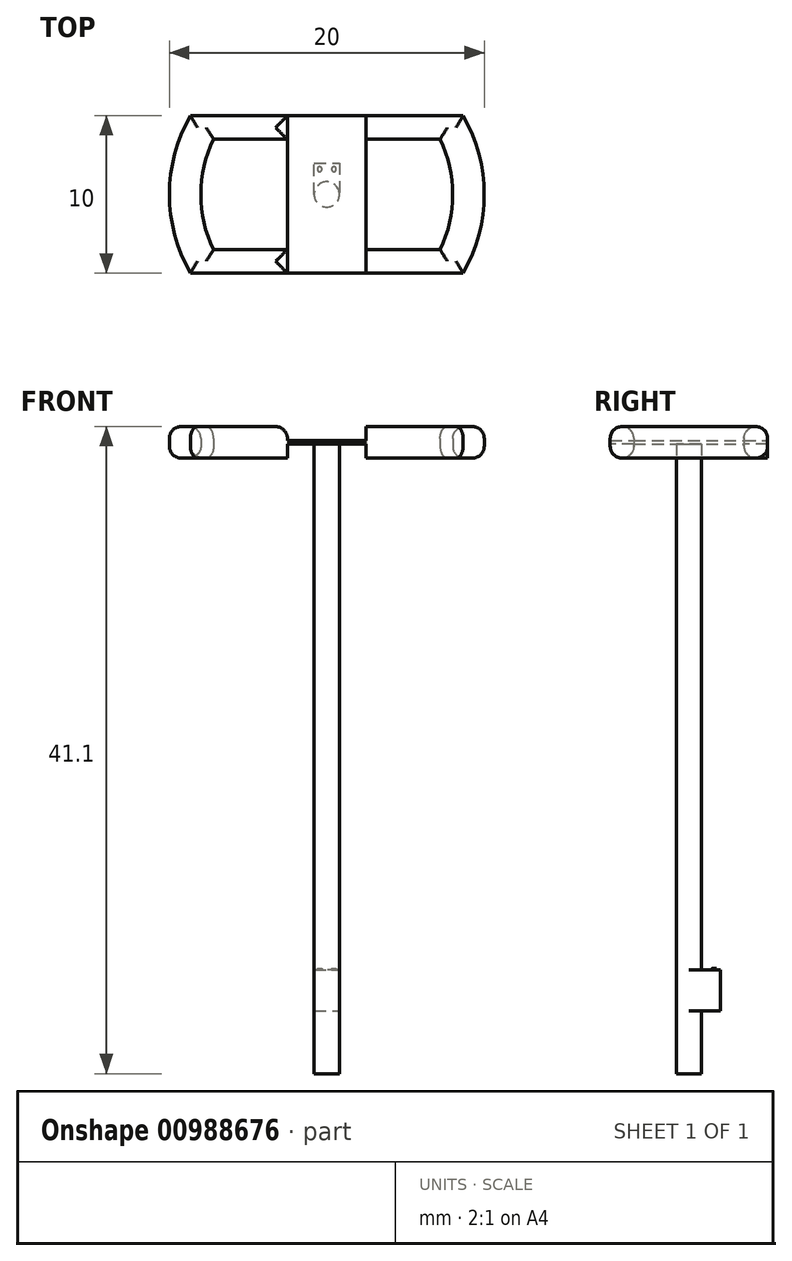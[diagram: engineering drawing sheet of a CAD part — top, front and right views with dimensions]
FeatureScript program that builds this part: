
annotation { "Feature Type Name" : "Feature", "Feature Type Description" : "" }
export const myFeature = defineFeature(function(context is Context, id is Id, definition is map)
    precondition{}
    {
        {
            var Q0;
            Q0=qCreatedBy(makeId("Top.planeOp"),FACE);
            var sketch = newSketch(context, id + "F0", { "sketchPlane" : qUnion([Q0])});
            skCircle(sketch, "E0", {"center": v(0, 0) * mm, "radius": 0.8 * mm});
            skSolve(sketch);
        }
        {
            var Q0;
            Q0=makeQuery(id+"F0.imprint","IMPRINT",FACE,{"disambiguationData":[TD([[makeQuery(id+"F0.imprint","IMPRINT",EDGE,{"derivedFrom":sQuery(id+"F0.wireOp",EDGE,"E0")}),1.0]])]});
            extrude(context, id + "F1", {"entities" : qUnion([Q0]), "depth" : 40 * mm, "offsetDistance" : 25 * mm});
        }
        {
            var Q0;
            Q0=makeQuery(id+"F1.opExtrude","CAP_FACE",FACE,{"disambiguationData":[OSD([sQuery(id+"F0.wireOp",EDGE,"E0")])],"isStart":true});
            var sketch = newSketch(context, id + "F2", { "sketchPlane" : qUnion([Q0])});
            skLineSegment(sketch, "E1", {"start": v(0, 0) * mm, "end": v(0.8, 0) * mm});
            skLineSegment(sketch, "E2", {"start": v(0.8, 0) * mm, "end": v(-0.8, 0) * mm});
            skLineSegment(sketch, "E3", {"start": v(-0.8, 0) * mm, "end": v(-0.8, -2) * mm});
            skLineSegment(sketch, "E4", {"start": v(-0.8, -2) * mm, "end": v(0.8, -2) * mm});
            skLineSegment(sketch, "E5", {"start": v(0.8, -2) * mm, "end": v(0.8, 0) * mm});
            skLineSegment(sketch, "E6", {"start": v(0, -2) * mm, "end": v(0, -0.8) * mm});
            skLineSegment(sketch, "E7", {"start": v(0.8, -1.2) * mm, "end": v(-0.8, -1.2) * mm});
            skPoint(sketch, "E8", {"position": v(-0.4, -1.6) * mm});
            skPoint(sketch, "E9", {"position": v(0.4, -1.6) * mm});
            skSolve(sketch);
        }
        {
            var Q0;
            {var subQ1=makeQuery(id+"F1.opExtrude","CAP_EDGE",EDGE,{"disambiguationData":[OSD([sQuery(id+"F0.wireOp",EDGE,"E0")])],"isStart":true});var subQ5=sQuery(id+"F2.wireOp",EDGE,"E6");var subQ6=makeQuery(id+"F2.imprint","INTERSECT",VERTEX,{"derivedFrom":[subQ1,subQ5]});Q0=makeQuery(id+"F2.imprint","IMPRINT",FACE,{"disambiguationData":[TD([[makeQuery(id+"F2.imprint","IMPRINT",EDGE,{"disambiguationData":[TD([[subQ6,1.0]])],"derivedFrom":subQ5}),-1.0]])]});}
            var Q1;
            {var subQ0=sQuery(id+"F2.wireOp",EDGE,"E5");var subQ1=sQuery(id+"F2.wireOp",EDGE,"E4");var subQ2=makeQuery(id+"F2.imprint","INTERSECT",VERTEX,{"derivedFrom":[subQ1,subQ0]});Q1=makeQuery(id+"F2.imprint","IMPRINT",FACE,{"disambiguationData":[TD([[makeQuery(id+"F2.imprint","IMPRINT",EDGE,{"disambiguationData":[TD([[subQ2,1.0]])],"derivedFrom":subQ1}),1.0]])]});}
            var Q2;
            {var subQ0=sQuery(id+"F2.wireOp",EDGE,"E4");var subQ1=sQuery(id+"F2.wireOp",EDGE,"E3");var subQ2=makeQuery(id+"F2.imprint","INTERSECT",VERTEX,{"derivedFrom":[subQ1,subQ0]});Q2=makeQuery(id+"F2.imprint","IMPRINT",FACE,{"disambiguationData":[TD([[makeQuery(id+"F2.imprint","IMPRINT",EDGE,{"disambiguationData":[TD([[subQ2,1.0]])],"derivedFrom":subQ1}),1.0]])]});}
            var Q3;
            {var subQ1=makeQuery(id+"F1.opExtrude","CAP_EDGE",EDGE,{"disambiguationData":[OSD([sQuery(id+"F0.wireOp",EDGE,"E0")])],"isStart":true});var subQ5=sQuery(id+"F2.wireOp",EDGE,"E6");var subQ6=makeQuery(id+"F2.imprint","INTERSECT",VERTEX,{"derivedFrom":[subQ1,subQ5]});Q3=makeQuery(id+"F2.imprint","IMPRINT",FACE,{"disambiguationData":[TD([[makeQuery(id+"F2.imprint","IMPRINT",EDGE,{"disambiguationData":[TD([[subQ6,1.0]])],"derivedFrom":subQ5}),1.0]])]});}
            extrude(context, id + "F3", {"entities" : qUnion([Q0, Q1, Q2, Q3]), "operationType" : NewBodyOperationType.ADD, "oppositeDirection" : true, "depth" : 4.15 * mm, "offsetDistance" : 25 * mm});
        }
        {
            var Q0;
            {var subQ0=sQuery(id+"F0.wireOp",EDGE,"E0");Q0=makeQuery(id+"F3.boolean.opBoolean","MERGE",FACE,{"derivedFrom":[makeQuery(id+"F1.opExtrude","CAP_FACE",FACE,{"disambiguationData":[OSD([subQ0])],"isStart":true}),makeQuery(id+"F3.opExtrude","CAP_FACE",FACE,{"disambiguationData":[OSD([subQ0,sQuery(id+"F2.wireOp",EDGE,"E3"),sQuery(id+"F2.wireOp",EDGE,"E4"),sQuery(id+"F2.wireOp",EDGE,"E5")])],"isStart":true})]});}
            var sketch = newSketch(context, id + "F4", { "sketchPlane" : qUnion([Q0])});
            skCircle(sketch, "E10", {"center": v(0, 0) * mm, "radius": 0.8 * mm});
            skSolve(sketch);
        }
        {
            var Q0;
            Q0=makeQuery(id+"F4.imprint","IMPRINT",FACE,{"disambiguationData":[TD([[makeQuery(id+"F4.imprint","IMPRINT",EDGE,{"disambiguationData":[OD(0.0)],"derivedFrom":sQuery(id+"F4.wireOp",EDGE,"E10")}),-1.0]])]});
            extrude(context, id + "F5", {"entities" : qUnion([Q0]), "operationType" : NewBodyOperationType.REMOVE, "oppositeDirection" : true, "depth" : 4 * mm, "offsetDistance" : 25 * mm});
        }
        {
            var Q0;
            Q0=makeQuery(id+"F3.opExtrude","CAP_FACE",FACE,{"disambiguationData":[OSD([sQuery(id+"F0.wireOp",EDGE,"E0"),sQuery(id+"F2.wireOp",EDGE,"E3"),sQuery(id+"F2.wireOp",EDGE,"E4"),sQuery(id+"F2.wireOp",EDGE,"E5")])],"isStart":false});
            extrude(context, id + "F6", {"entities" : qUnion([Q0]), "operationType" : NewBodyOperationType.ADD, "depth" : 2.43 * mm, "offsetDistance" : 25 * mm});
        }
        {
            var Q0;
            Q0=makeQuery(id+"F6.opExtrude","CAP_FACE",FACE,{"disambiguationData":[OSD([sQuery(id+"F0.wireOp",EDGE,"E0"),sQuery(id+"F2.wireOp",EDGE,"E3"),sQuery(id+"F2.wireOp",EDGE,"E4"),sQuery(id+"F2.wireOp",EDGE,"E5")])],"isStart":false});
            var sketch = newSketch(context, id + "F7", { "sketchPlane" : qUnion([Q0])});
            skLineSegment(sketch, "E11", {"start": v(-0.8, 1.4) * mm, "end": v(0.8, 1.4) * mm});
            skLineSegment(sketch, "E12", {"start": v(0, 1.4) * mm, "end": v(0, 2) * mm});
            skPoint(sketch, "E13", {"position": v(-0.45, 1.6) * mm});
            skPoint(sketch, "E14", {"position": v(0.45, 1.6) * mm});
            skCircle(sketch, "E15", {"center": v(-0.45, 1.6) * mm, "radius": 0.15 * mm});
            skCircle(sketch, "E16", {"center": v(0.45, 1.6) * mm, "radius": 0.15 * mm});
            skSolve(sketch);
        }
        {
            var Q0;
            Q0=makeQuery(id+"F7.imprint","IMPRINT",FACE,{"disambiguationData":[TD([[makeQuery(id+"F7.imprint","IMPRINT",EDGE,{"derivedFrom":sQuery(id+"F7.wireOp",EDGE,"E16")}),1.0]])]});
            var Q1;
            Q1=makeQuery(id+"F7.imprint","IMPRINT",FACE,{"disambiguationData":[TD([[makeQuery(id+"F7.imprint","IMPRINT",EDGE,{"derivedFrom":sQuery(id+"F7.wireOp",EDGE,"E15")}),1.0]])]});
            extrude(context, id + "F8", {"entities" : qUnion([Q0, Q1]), "operationType" : NewBodyOperationType.ADD, "depth" : 0.1 * mm, "offsetDistance" : 25 * mm});
        }
        {
            var Q0;
            Q0=makeQuery(id+"F1.opExtrude","CAP_FACE",FACE,{"disambiguationData":[OSD([sQuery(id+"F0.wireOp",EDGE,"E0")])],"isStart":false});
            var sketch = newSketch(context, id + "F9", { "sketchPlane" : qUnion([Q0])});
            skCircle(sketch, "E17", {"center": v(0, 0) * mm, "radius": 10 * mm});
            skLineSegment(sketch, "E18", {"start": v(0, 0) * mm, "end": v(10, 0) * mm});
            skLineSegment(sketch, "E19", {"start": v(0, 0) * mm, "end": v(-10, 0) * mm});
            skLineSegment(sketch, "E20", {"start": v(-8.66, -5) * mm, "end": v(8.66, -5) * mm});
            skLineSegment(sketch, "E21", {"start": v(-8.66, 5) * mm, "end": v(8.66, 5) * mm});
            skCircle(sketch, "E22", {"center": v(0, 0) * mm, "radius": 8 * mm});
            skLineSegment(sketch, "E23", {"start": v(9.37, -3.5) * mm, "end": v(-9.37, -3.5) * mm});
            skLineSegment(sketch, "E24", {"start": v(9.37, 3.5) * mm, "end": v(-9.37, 3.5) * mm});
            skCircle(sketch, "E25", {"center": v(0, 0) * mm, "radius": 0.8 * mm});
            skLineSegment(sketch, "E26.bottom", {"start": v(2.5, -5) * mm, "end": v(-2.5, -5) * mm});
            skLineSegment(sketch, "E26.top", {"start": v(2.5, 5) * mm, "end": v(-2.5, 5) * mm});
            skLineSegment(sketch, "E26.left", {"start": v(2.5, -5) * mm, "end": v(2.5, 5) * mm});
            skLineSegment(sketch, "E26.right", {"start": v(-2.5, -5) * mm, "end": v(-2.5, 5) * mm});
            skSolve(sketch);
        }
        {
            var Q0;
            {var subQ0=sQuery(id+"F9.wireOp",EDGE,"E26.right");var subQ1=sQuery(id+"F9.wireOp",EDGE,"E20");var subQ2=makeQuery(id+"F9.imprint","INTERSECT",VERTEX,{"derivedFrom":[subQ1,subQ0]});Q0=makeQuery(id+"F9.imprint","IMPRINT",FACE,{"disambiguationData":[TD([[makeQuery(id+"F9.imprint","IMPRINT",EDGE,{"disambiguationData":[TD([[subQ2,1.0]])],"derivedFrom":subQ1}),1.0]])]});}
            var Q1;
            {var subQ0=sQuery(id+"F9.wireOp",EDGE,"E26.right");var subQ1=sQuery(id+"F9.wireOp",EDGE,"E20");var subQ2=makeQuery(id+"F9.imprint","INTERSECT",VERTEX,{"derivedFrom":[subQ1,subQ0]});Q1=makeQuery(id+"F9.imprint","IMPRINT",FACE,{"disambiguationData":[TD([[makeQuery(id+"F9.imprint","IMPRINT",EDGE,{"disambiguationData":[TD([[subQ2,-1.0]])],"derivedFrom":subQ1}),1.0]])]});}
            var Q2;
            {var subQ1=sQuery(id+"F9.wireOp",EDGE,"E18");var subQ5=sQuery(id+"F9.wireOp",EDGE,"E26.left");var subQ11=makeQuery(id+"F9.imprint","INTERSECT",VERTEX,{"derivedFrom":[subQ1,subQ5]});Q2=makeQuery(id+"F9.imprint","IMPRINT",FACE,{"disambiguationData":[TD([[makeQuery(id+"F9.imprint","IMPRINT",EDGE,{"disambiguationData":[TD([[subQ11,1.0]])],"derivedFrom":subQ1}),-1.0]])]});}
            var Q3;
            {var subQ1=sQuery(id+"F9.wireOp",EDGE,"E18");var subQ5=sQuery(id+"F9.wireOp",EDGE,"E26.left");var subQ11=makeQuery(id+"F9.imprint","INTERSECT",VERTEX,{"derivedFrom":[subQ1,subQ5]});Q3=makeQuery(id+"F9.imprint","IMPRINT",FACE,{"disambiguationData":[TD([[makeQuery(id+"F9.imprint","IMPRINT",EDGE,{"disambiguationData":[TD([[subQ11,1.0]])],"derivedFrom":subQ1}),1.0]])]});}
            var Q4;
            {var subQ0=sQuery(id+"F9.wireOp",EDGE,"E25");var subQ1=sQuery(id+"F9.wireOp",EDGE,"E18");var subQ2=makeQuery(id+"F9.imprint","INTERSECT",VERTEX,{"derivedFrom":[subQ1,subQ0]});Q4=makeQuery(id+"F9.imprint","IMPRINT",FACE,{"disambiguationData":[TD([[makeQuery(id+"F9.imprint","IMPRINT",EDGE,{"disambiguationData":[TD([[subQ2,1.0]])],"derivedFrom":subQ1}),1.0]])]});}
            var Q5;
            {var subQ0=sQuery(id+"F9.wireOp",EDGE,"E25");var subQ1=sQuery(id+"F9.wireOp",EDGE,"E18");var subQ2=makeQuery(id+"F9.imprint","INTERSECT",VERTEX,{"derivedFrom":[subQ1,subQ0]});Q5=makeQuery(id+"F9.imprint","IMPRINT",FACE,{"disambiguationData":[TD([[makeQuery(id+"F9.imprint","IMPRINT",EDGE,{"disambiguationData":[TD([[subQ2,1.0]])],"derivedFrom":subQ1}),-1.0]])]});}
            var Q6;
            {var subQ0=sQuery(id+"F9.wireOp",EDGE,"E26.left");var subQ1=sQuery(id+"F9.wireOp",EDGE,"E20");var subQ2=makeQuery(id+"F9.imprint","INTERSECT",VERTEX,{"derivedFrom":[subQ1,subQ0]});Q6=makeQuery(id+"F9.imprint","IMPRINT",FACE,{"disambiguationData":[TD([[makeQuery(id+"F9.imprint","IMPRINT",EDGE,{"disambiguationData":[TD([[subQ2,-1.0]])],"derivedFrom":subQ1}),1.0]])]});}
            var Q7;
            {var subQ0=sQuery(id+"F9.wireOp",EDGE,"E26.left");var subQ1=sQuery(id+"F9.wireOp",EDGE,"E21");var subQ2=makeQuery(id+"F9.imprint","INTERSECT",VERTEX,{"derivedFrom":[subQ1,subQ0]});Q7=makeQuery(id+"F9.imprint","IMPRINT",FACE,{"disambiguationData":[TD([[makeQuery(id+"F9.imprint","IMPRINT",EDGE,{"disambiguationData":[TD([[subQ2,-1.0]])],"derivedFrom":subQ1}),-1.0]])]});}
            var Q8;
            {var subQ0=sQuery(id+"F9.wireOp",EDGE,"E26.right");var subQ1=sQuery(id+"F9.wireOp",EDGE,"E21");var subQ2=makeQuery(id+"F9.imprint","INTERSECT",VERTEX,{"derivedFrom":[subQ1,subQ0]});Q8=makeQuery(id+"F9.imprint","IMPRINT",FACE,{"disambiguationData":[TD([[makeQuery(id+"F9.imprint","IMPRINT",EDGE,{"disambiguationData":[TD([[subQ2,-1.0]])],"derivedFrom":subQ1}),-1.0]])]});}
            var Q9;
            {var subQ0=sQuery(id+"F9.wireOp",EDGE,"E26.right");var subQ1=sQuery(id+"F9.wireOp",EDGE,"E21");var subQ2=makeQuery(id+"F9.imprint","INTERSECT",VERTEX,{"derivedFrom":[subQ1,subQ0]});Q9=makeQuery(id+"F9.imprint","IMPRINT",FACE,{"disambiguationData":[TD([[makeQuery(id+"F9.imprint","IMPRINT",EDGE,{"disambiguationData":[TD([[subQ2,1.0]])],"derivedFrom":subQ1}),-1.0]])]});}
            var Q10;
            {var subQ0=sQuery(id+"F9.wireOp",EDGE,"E23");var subQ1=sQuery(id+"F9.wireOp",EDGE,"E17");var subQ2=makeQuery(id+"F9.imprint","INTERSECT",VERTEX,{"disambiguationData":[OD(0.0)],"derivedFrom":[subQ1,subQ0]});Q10=makeQuery(id+"F9.imprint","IMPRINT",FACE,{"disambiguationData":[TD([[makeQuery(id+"F9.imprint","IMPRINT",EDGE,{"disambiguationData":[TD([[subQ2,-1.0]])],"derivedFrom":subQ1}),1.0]])]});}
            var Q11;
            {var subQ0=sQuery(id+"F9.wireOp",EDGE,"E23");var subQ1=sQuery(id+"F9.wireOp",EDGE,"E17");var subQ2=makeQuery(id+"F9.imprint","INTERSECT",VERTEX,{"disambiguationData":[OD(0.0)],"derivedFrom":[subQ1,subQ0]});Q11=makeQuery(id+"F9.imprint","IMPRINT",FACE,{"disambiguationData":[TD([[makeQuery(id+"F9.imprint","IMPRINT",EDGE,{"disambiguationData":[TD([[subQ2,1.0]])],"derivedFrom":subQ1}),1.0]])]});}
            var Q12;
            {var subQ0=sQuery(id+"F9.wireOp",EDGE,"E24");var subQ1=sQuery(id+"F9.wireOp",EDGE,"E17");var subQ2=makeQuery(id+"F9.imprint","INTERSECT",VERTEX,{"disambiguationData":[OD(0.0)],"derivedFrom":[subQ1,subQ0]});Q12=makeQuery(id+"F9.imprint","IMPRINT",FACE,{"disambiguationData":[TD([[makeQuery(id+"F9.imprint","IMPRINT",EDGE,{"disambiguationData":[TD([[subQ2,-1.0]])],"derivedFrom":subQ1}),1.0]])]});}
            var Q13;
            {var subQ0=sQuery(id+"F9.wireOp",EDGE,"E24");var subQ1=sQuery(id+"F9.wireOp",EDGE,"E17");var subQ2=makeQuery(id+"F9.imprint","INTERSECT",VERTEX,{"disambiguationData":[OD(0.0)],"derivedFrom":[subQ1,subQ0]});Q13=makeQuery(id+"F9.imprint","IMPRINT",FACE,{"disambiguationData":[TD([[makeQuery(id+"F9.imprint","IMPRINT",EDGE,{"disambiguationData":[TD([[subQ2,1.0]])],"derivedFrom":subQ1}),1.0]])]});}
            var Q14;
            {var subQ0=sQuery(id+"F9.wireOp",EDGE,"E20");var subQ1=sQuery(id+"F9.wireOp",EDGE,"E17");var subQ2=makeQuery(id+"F9.imprint","INTERSECT",VERTEX,{"disambiguationData":[OD(0.0)],"derivedFrom":[subQ1,subQ0]});Q14=makeQuery(id+"F9.imprint","IMPRINT",FACE,{"disambiguationData":[TD([[makeQuery(id+"F9.imprint","IMPRINT",EDGE,{"disambiguationData":[TD([[subQ2,-1.0]])],"derivedFrom":subQ1}),1.0]])]});}
            var Q15;
            {var subQ0=sQuery(id+"F9.wireOp",EDGE,"E18");var subQ1=sQuery(id+"F9.wireOp",EDGE,"E17");var subQ2=makeQuery(id+"F9.imprint","INTERSECT",VERTEX,{"derivedFrom":[subQ1,subQ0]});Q15=makeQuery(id+"F9.imprint","IMPRINT",FACE,{"disambiguationData":[TD([[makeQuery(id+"F9.imprint","IMPRINT",EDGE,{"disambiguationData":[TD([[subQ2,1.0]])],"derivedFrom":subQ1}),1.0]])]});}
            var Q16;
            {var subQ0=sQuery(id+"F9.wireOp",EDGE,"E24");var subQ1=sQuery(id+"F9.wireOp",EDGE,"E17");var subQ2=makeQuery(id+"F9.imprint","INTERSECT",VERTEX,{"disambiguationData":[OD(1.0)],"derivedFrom":[subQ1,subQ0]});Q16=makeQuery(id+"F9.imprint","IMPRINT",FACE,{"disambiguationData":[TD([[makeQuery(id+"F9.imprint","IMPRINT",EDGE,{"disambiguationData":[TD([[subQ2,1.0]])],"derivedFrom":subQ1}),1.0]])]});}
            var Q17;
            {var subQ0=sQuery(id+"F9.wireOp",EDGE,"E21");var subQ1=sQuery(id+"F9.wireOp",EDGE,"E17");var subQ2=makeQuery(id+"F9.imprint","INTERSECT",VERTEX,{"disambiguationData":[OD(0.0)],"derivedFrom":[subQ1,subQ0]});Q17=makeQuery(id+"F9.imprint","IMPRINT",FACE,{"disambiguationData":[TD([[makeQuery(id+"F9.imprint","IMPRINT",EDGE,{"disambiguationData":[TD([[subQ2,1.0]])],"derivedFrom":subQ1}),1.0]])]});}
            extrude(context, id + "F10", {"entities" : qUnion([Q0, Q1, Q2, Q3, Q4, Q5, Q6, Q7, Q8, Q9, Q10, Q11, Q12, Q13, Q14, Q15, Q16, Q17]), "operationType" : NewBodyOperationType.ADD, "depth" : 0.2 * mm, "offsetDistance" : 25 * mm});
        }
        {
            var Q0;
            Q0=makeQuery(id+"F10.opExtrude","CAP_FACE",FACE,{"disambiguationData":[OSD([sQuery(id+"F9.wireOp",EDGE,"E17"),sQuery(id+"F9.wireOp",EDGE,"E20"),sQuery(id+"F9.wireOp",EDGE,"E21"),sQuery(id+"F9.wireOp",EDGE,"E22"),sQuery(id+"F9.wireOp",EDGE,"E23"),sQuery(id+"F9.wireOp",EDGE,"E24"),sQuery(id+"F9.wireOp",EDGE,"E26.left"),sQuery(id+"F9.wireOp",EDGE,"E26.right")])],"isStart":false});
            var sketch = newSketch(context, id + "F11", { "sketchPlane" : qUnion([Q0])});
            skLineSegment(sketch, "E27", {"start": v(2.5, -5) * mm, "end": v(2.5, 5) * mm});
            skLineSegment(sketch, "E28", {"start": v(-2.5, -5) * mm, "end": v(-2.5, 5) * mm});
            skSolve(sketch);
        }
        {
            var Q0;
            {var subQ3=sQuery(id+"F9.wireOp",EDGE,"E23");var subQ17=sQuery(id+"F9.wireOp",EDGE,"E26.right");var subQ19=makeQuery(id+"F10.opExtrude","CAP_EDGE",EDGE,{"disambiguationData":[OSD([subQ3]),TDD([makeQuery(id+"F9.imprint","IMPRINT",EDGE,{"disambiguationData":[TD([[makeQuery(id+"F9.imprint","INTERSECT",VERTEX,{"derivedFrom":[subQ3,subQ17]}),-1.0]])],"derivedFrom":subQ3})])],"isStart":false});Q0=makeQuery(id+"F11.imprint","IMPRINT",FACE,{"disambiguationData":[TD([[makeQuery(id+"F11.imprint","IMPRINT",EDGE,{"derivedFrom":subQ19}),1.0]])]});}
            var Q1;
            {var subQ3=sQuery(id+"F9.wireOp",EDGE,"E23");var subQ17=sQuery(id+"F9.wireOp",EDGE,"E26.left");var subQ19=makeQuery(id+"F10.opExtrude","CAP_EDGE",EDGE,{"disambiguationData":[OSD([subQ3]),TDD([makeQuery(id+"F9.imprint","IMPRINT",EDGE,{"disambiguationData":[TD([[makeQuery(id+"F9.imprint","INTERSECT",VERTEX,{"derivedFrom":[subQ3,subQ17]}),1.0]])],"derivedFrom":subQ3})])],"isStart":false});Q1=makeQuery(id+"F11.imprint","IMPRINT",FACE,{"disambiguationData":[TD([[makeQuery(id+"F11.imprint","IMPRINT",EDGE,{"derivedFrom":subQ19}),1.0]])]});}
            extrude(context, id + "F12", {"entities" : qUnion([Q0, Q1]), "operationType" : NewBodyOperationType.ADD, "depth" : 0.9 * mm, "offsetDistance" : 25 * mm});
        }
        {
            var Q0;
            Q0=makeQuery(id+"F10.opExtrude","CAP_FACE",FACE,{"disambiguationData":[OSD([sQuery(id+"F9.wireOp",EDGE,"E17"),sQuery(id+"F9.wireOp",EDGE,"E20"),sQuery(id+"F9.wireOp",EDGE,"E21"),sQuery(id+"F9.wireOp",EDGE,"E22"),sQuery(id+"F9.wireOp",EDGE,"E23"),sQuery(id+"F9.wireOp",EDGE,"E24"),sQuery(id+"F9.wireOp",EDGE,"E26.left"),sQuery(id+"F9.wireOp",EDGE,"E26.right")])],"isStart":true});
            var sketch = newSketch(context, id + "F13", { "sketchPlane" : qUnion([Q0])});
            skLineSegment(sketch, "E29", {"start": v(2.5, -5) * mm, "end": v(2.5, 5) * mm});
            skLineSegment(sketch, "E30", {"start": v(-2.5, -5) * mm, "end": v(-2.5, 5) * mm});
            skSolve(sketch);
        }
        {
            var Q0;
            {var subQ3=sQuery(id+"F9.wireOp",EDGE,"E23");var subQ15=sQuery(id+"F9.wireOp",EDGE,"E26.left");var subQ16=makeQuery(id+"F10.opExtrude","CAP_EDGE",EDGE,{"disambiguationData":[OSD([subQ3]),TDD([makeQuery(id+"F9.imprint","IMPRINT",EDGE,{"disambiguationData":[TD([[makeQuery(id+"F9.imprint","INTERSECT",VERTEX,{"derivedFrom":[subQ3,subQ15]}),1.0]])],"derivedFrom":subQ3})])],"isStart":true});Q0=makeQuery(id+"F13.imprint","IMPRINT",FACE,{"disambiguationData":[TD([[makeQuery(id+"F13.imprint","IMPRINT",EDGE,{"derivedFrom":subQ16}),-1.0]])]});}
            var Q1;
            {var subQ3=sQuery(id+"F9.wireOp",EDGE,"E23");var subQ15=sQuery(id+"F9.wireOp",EDGE,"E26.right");var subQ16=makeQuery(id+"F10.opExtrude","CAP_EDGE",EDGE,{"disambiguationData":[OSD([subQ3]),TDD([makeQuery(id+"F9.imprint","IMPRINT",EDGE,{"disambiguationData":[TD([[makeQuery(id+"F9.imprint","INTERSECT",VERTEX,{"derivedFrom":[subQ3,subQ15]}),-1.0]])],"derivedFrom":subQ3})])],"isStart":true});Q1=makeQuery(id+"F13.imprint","IMPRINT",FACE,{"disambiguationData":[TD([[makeQuery(id+"F13.imprint","IMPRINT",EDGE,{"derivedFrom":subQ16}),-1.0]])]});}
            extrude(context, id + "F14", {"entities" : qUnion([Q0, Q1]), "operationType" : NewBodyOperationType.ADD, "depth" : 0.9 * mm, "offsetDistance" : 25 * mm});
        }
        {
            var Q0;
            {var subQ0=sQuery(id+"F9.wireOp",EDGE,"E17");var subQ1=makeQuery(id+"F9.imprint","INTERSECT",VERTEX,{"derivedFrom":[subQ0,sQuery(id+"F9.wireOp",EDGE,"E18")]});var subQ3=makeQuery(id+"F9.imprint","INTERSECT",VERTEX,{"disambiguationData":[OD(1.0)],"derivedFrom":[subQ0,sQuery(id+"F9.wireOp",EDGE,"E24")]});Q0=makeQuery(id+"F12.opExtrude","CAP_EDGE",EDGE,{"disambiguationData":[OSD([subQ0]),TDD([makeQuery(id+"F11.imprint","IMPRINT",EDGE,{"derivedFrom":makeQuery(id+"F10.opExtrude","CAP_EDGE",EDGE,{"disambiguationData":[OSD([subQ0]),TDD([makeQuery(id+"F9.imprint","IMPRINT",EDGE,{"disambiguationData":[TD([[subQ3,1.0]])],"derivedFrom":subQ0}),makeQuery(id+"F9.imprint","IMPRINT",EDGE,{"disambiguationData":[TD([[makeQuery(id+"F9.imprint","INTERSECT",VERTEX,{"disambiguationData":[OD(0.0)],"derivedFrom":[subQ0,sQuery(id+"F9.wireOp",EDGE,"E21")]}),1.0]])],"derivedFrom":subQ0}),makeQuery(id+"F9.imprint","IMPRINT",EDGE,{"disambiguationData":[TD([[makeQuery(id+"F9.imprint","INTERSECT",VERTEX,{"disambiguationData":[OD(0.0)],"derivedFrom":[subQ0,sQuery(id+"F9.wireOp",EDGE,"E20")]}),-1.0]])],"derivedFrom":subQ0}),makeQuery(id+"F9.imprint","IMPRINT",EDGE,{"disambiguationData":[TD([[subQ1,1.0]])],"derivedFrom":subQ0})])],"isStart":false})})])],"isStart":false});}
            var Q1;
            {var subQ0=sQuery(id+"F9.wireOp",EDGE,"E22");var subQ1=makeQuery(id+"F9.imprint","INTERSECT",VERTEX,{"derivedFrom":[sQuery(id+"F9.wireOp",EDGE,"E18"),subQ0]});Q1=makeQuery(id+"F12.opExtrude","CAP_EDGE",EDGE,{"disambiguationData":[OSD([subQ0]),TDD([makeQuery(id+"F11.imprint","IMPRINT",EDGE,{"derivedFrom":makeQuery(id+"F10.opExtrude","CAP_EDGE",EDGE,{"disambiguationData":[OSD([subQ0]),TDD([makeQuery(id+"F9.imprint","IMPRINT",EDGE,{"disambiguationData":[TD([[subQ1,-1.0]])],"derivedFrom":subQ0}),makeQuery(id+"F9.imprint","IMPRINT",EDGE,{"disambiguationData":[TD([[subQ1,1.0]])],"derivedFrom":subQ0})])],"isStart":false})})])],"isStart":false});}
            var Q2;
            {var subQ0=sQuery(id+"F9.wireOp",EDGE,"E17");var subQ1=makeQuery(id+"F9.imprint","INTERSECT",VERTEX,{"derivedFrom":[subQ0,sQuery(id+"F9.wireOp",EDGE,"E18")]});var subQ3=makeQuery(id+"F9.imprint","INTERSECT",VERTEX,{"disambiguationData":[OD(1.0)],"derivedFrom":[subQ0,sQuery(id+"F9.wireOp",EDGE,"E24")]});Q2=makeQuery(id+"F14.opExtrude","CAP_EDGE",EDGE,{"disambiguationData":[OSD([subQ0]),TDD([makeQuery(id+"F13.imprint","IMPRINT",EDGE,{"derivedFrom":makeQuery(id+"F10.opExtrude","CAP_EDGE",EDGE,{"disambiguationData":[OSD([subQ0]),TDD([makeQuery(id+"F9.imprint","IMPRINT",EDGE,{"disambiguationData":[TD([[subQ3,1.0]])],"derivedFrom":subQ0}),makeQuery(id+"F9.imprint","IMPRINT",EDGE,{"disambiguationData":[TD([[makeQuery(id+"F9.imprint","INTERSECT",VERTEX,{"disambiguationData":[OD(0.0)],"derivedFrom":[subQ0,sQuery(id+"F9.wireOp",EDGE,"E21")]}),1.0]])],"derivedFrom":subQ0}),makeQuery(id+"F9.imprint","IMPRINT",EDGE,{"disambiguationData":[TD([[makeQuery(id+"F9.imprint","INTERSECT",VERTEX,{"disambiguationData":[OD(0.0)],"derivedFrom":[subQ0,sQuery(id+"F9.wireOp",EDGE,"E20")]}),-1.0]])],"derivedFrom":subQ0}),makeQuery(id+"F9.imprint","IMPRINT",EDGE,{"disambiguationData":[TD([[subQ1,1.0]])],"derivedFrom":subQ0})])],"isStart":true})})])],"isStart":false});}
            var Q3;
            {var subQ0=sQuery(id+"F9.wireOp",EDGE,"E22");var subQ1=makeQuery(id+"F9.imprint","INTERSECT",VERTEX,{"derivedFrom":[sQuery(id+"F9.wireOp",EDGE,"E18"),subQ0]});Q3=makeQuery(id+"F14.opExtrude","CAP_EDGE",EDGE,{"disambiguationData":[OSD([subQ0]),TDD([makeQuery(id+"F13.imprint","IMPRINT",EDGE,{"derivedFrom":makeQuery(id+"F10.opExtrude","CAP_EDGE",EDGE,{"disambiguationData":[OSD([subQ0]),TDD([makeQuery(id+"F9.imprint","IMPRINT",EDGE,{"disambiguationData":[TD([[subQ1,-1.0]])],"derivedFrom":subQ0}),makeQuery(id+"F9.imprint","IMPRINT",EDGE,{"disambiguationData":[TD([[subQ1,1.0]])],"derivedFrom":subQ0})])],"isStart":true})})])],"isStart":false});}
            var Q4;
            {var subQ0=sQuery(id+"F9.wireOp",EDGE,"E24");Q4=makeQuery(id+"F12.opExtrude","CAP_EDGE",EDGE,{"disambiguationData":[OSD([subQ0]),TDD([makeQuery(id+"F11.imprint","IMPRINT",EDGE,{"derivedFrom":makeQuery(id+"F10.opExtrude","CAP_EDGE",EDGE,{"disambiguationData":[OSD([subQ0]),TDD([makeQuery(id+"F9.imprint","IMPRINT",EDGE,{"disambiguationData":[TD([[makeQuery(id+"F9.imprint","INTERSECT",VERTEX,{"derivedFrom":[subQ0,sQuery(id+"F9.wireOp",EDGE,"E26.left")]}),1.0]])],"derivedFrom":subQ0})])],"isStart":false})})])],"isStart":false});}
            var Q5;
            {var subQ0=sQuery(id+"F9.wireOp",EDGE,"E21");var subQ1=makeQuery(id+"F10.opExtrude","CAP_EDGE",EDGE,{"disambiguationData":[OSD([subQ0])],"isStart":false});Q5=makeQuery(id+"F12.opExtrude","CAP_EDGE",EDGE,{"disambiguationData":[OSD([subQ0]),TDD([makeQuery(id+"F11.imprint","IMPRINT",EDGE,{"disambiguationData":[TD([[makeQuery(id+"F11.imprint","INTERSECT",VERTEX,{"derivedFrom":[subQ1,sQuery(id+"F11.wireOp",EDGE,"E27")]}),-1.0]])],"derivedFrom":subQ1})])],"isStart":false});}
            var Q6;
            {var subQ0=sQuery(id+"F9.wireOp",EDGE,"E21");var subQ1=makeQuery(id+"F10.opExtrude","CAP_EDGE",EDGE,{"disambiguationData":[OSD([subQ0])],"isStart":true});Q6=makeQuery(id+"F14.opExtrude","CAP_EDGE",EDGE,{"disambiguationData":[OSD([subQ0]),TDD([makeQuery(id+"F13.imprint","IMPRINT",EDGE,{"disambiguationData":[TD([[makeQuery(id+"F13.imprint","INTERSECT",VERTEX,{"derivedFrom":[subQ1,sQuery(id+"F13.wireOp",EDGE,"E29")]}),-1.0]])],"derivedFrom":subQ1})])],"isStart":false});}
            var Q7;
            {var subQ0=sQuery(id+"F9.wireOp",EDGE,"E24");Q7=makeQuery(id+"F14.opExtrude","CAP_EDGE",EDGE,{"disambiguationData":[OSD([subQ0]),TDD([makeQuery(id+"F13.imprint","IMPRINT",EDGE,{"derivedFrom":makeQuery(id+"F10.opExtrude","CAP_EDGE",EDGE,{"disambiguationData":[OSD([subQ0]),TDD([makeQuery(id+"F9.imprint","IMPRINT",EDGE,{"disambiguationData":[TD([[makeQuery(id+"F9.imprint","INTERSECT",VERTEX,{"derivedFrom":[subQ0,sQuery(id+"F9.wireOp",EDGE,"E26.left")]}),1.0]])],"derivedFrom":subQ0})])],"isStart":true})})])],"isStart":false});}
            var Q8;
            {var subQ0=sQuery(id+"F9.wireOp",EDGE,"E23");Q8=makeQuery(id+"F14.opExtrude","CAP_EDGE",EDGE,{"disambiguationData":[OSD([subQ0]),TDD([makeQuery(id+"F13.imprint","IMPRINT",EDGE,{"derivedFrom":makeQuery(id+"F10.opExtrude","CAP_EDGE",EDGE,{"disambiguationData":[OSD([subQ0]),TDD([makeQuery(id+"F9.imprint","IMPRINT",EDGE,{"disambiguationData":[TD([[makeQuery(id+"F9.imprint","INTERSECT",VERTEX,{"derivedFrom":[subQ0,sQuery(id+"F9.wireOp",EDGE,"E26.left")]}),1.0]])],"derivedFrom":subQ0})])],"isStart":true})})])],"isStart":false});}
            var Q9;
            {var subQ0=sQuery(id+"F9.wireOp",EDGE,"E20");var subQ1=makeQuery(id+"F10.opExtrude","CAP_EDGE",EDGE,{"disambiguationData":[OSD([subQ0])],"isStart":true});Q9=makeQuery(id+"F14.opExtrude","CAP_EDGE",EDGE,{"disambiguationData":[OSD([subQ0]),TDD([makeQuery(id+"F13.imprint","IMPRINT",EDGE,{"disambiguationData":[TD([[makeQuery(id+"F13.imprint","INTERSECT",VERTEX,{"derivedFrom":[subQ1,sQuery(id+"F13.wireOp",EDGE,"E29")]}),-1.0]])],"derivedFrom":subQ1})])],"isStart":false});}
            var Q10;
            {var subQ0=sQuery(id+"F9.wireOp",EDGE,"E20");var subQ1=makeQuery(id+"F10.opExtrude","CAP_EDGE",EDGE,{"disambiguationData":[OSD([subQ0])],"isStart":false});Q10=makeQuery(id+"F12.opExtrude","CAP_EDGE",EDGE,{"disambiguationData":[OSD([subQ0]),TDD([makeQuery(id+"F11.imprint","IMPRINT",EDGE,{"disambiguationData":[TD([[makeQuery(id+"F11.imprint","INTERSECT",VERTEX,{"derivedFrom":[subQ1,sQuery(id+"F11.wireOp",EDGE,"E27")]}),-1.0]])],"derivedFrom":subQ1})])],"isStart":false});}
            var Q11;
            {var subQ0=sQuery(id+"F9.wireOp",EDGE,"E23");Q11=makeQuery(id+"F12.opExtrude","CAP_EDGE",EDGE,{"disambiguationData":[OSD([subQ0]),TDD([makeQuery(id+"F11.imprint","IMPRINT",EDGE,{"derivedFrom":makeQuery(id+"F10.opExtrude","CAP_EDGE",EDGE,{"disambiguationData":[OSD([subQ0]),TDD([makeQuery(id+"F9.imprint","IMPRINT",EDGE,{"disambiguationData":[TD([[makeQuery(id+"F9.imprint","INTERSECT",VERTEX,{"derivedFrom":[subQ0,sQuery(id+"F9.wireOp",EDGE,"E26.left")]}),1.0]])],"derivedFrom":subQ0})])],"isStart":false})})])],"isStart":false});}
            fillet(context, id + "F15", {"entities" : qUnion([Q0, Q1, Q2, Q3, Q4, Q5, Q6, Q7, Q8, Q9, Q10, Q11]), "radius" : 0.75 * mm, "tangentPropagation" : true, "allowEdgeOverflow" : false});
        }
        {
            var Q0;
            {var subQ0=sQuery(id+"F9.wireOp",EDGE,"E23");Q0=makeQuery(id+"F12.opExtrude","CAP_EDGE",EDGE,{"disambiguationData":[OSD([subQ0]),TDD([makeQuery(id+"F11.imprint","IMPRINT",EDGE,{"derivedFrom":makeQuery(id+"F10.opExtrude","CAP_EDGE",EDGE,{"disambiguationData":[OSD([subQ0]),TDD([makeQuery(id+"F9.imprint","IMPRINT",EDGE,{"disambiguationData":[TD([[makeQuery(id+"F9.imprint","INTERSECT",VERTEX,{"derivedFrom":[subQ0,sQuery(id+"F9.wireOp",EDGE,"E26.right")]}),-1.0]])],"derivedFrom":subQ0})])],"isStart":false})})])],"isStart":false});}
            var Q1;
            {var subQ0=sQuery(id+"F9.wireOp",EDGE,"E20");var subQ1=makeQuery(id+"F10.opExtrude","CAP_EDGE",EDGE,{"disambiguationData":[OSD([subQ0])],"isStart":false});Q1=makeQuery(id+"F12.opExtrude","CAP_EDGE",EDGE,{"disambiguationData":[OSD([subQ0]),TDD([makeQuery(id+"F11.imprint","IMPRINT",EDGE,{"disambiguationData":[TD([[makeQuery(id+"F11.imprint","INTERSECT",VERTEX,{"derivedFrom":[subQ1,sQuery(id+"F11.wireOp",EDGE,"E28")]}),1.0]])],"derivedFrom":subQ1})])],"isStart":false});}
            var Q2;
            {var subQ0=sQuery(id+"F9.wireOp",EDGE,"E23");Q2=makeQuery(id+"F14.opExtrude","CAP_EDGE",EDGE,{"disambiguationData":[OSD([subQ0]),TDD([makeQuery(id+"F13.imprint","IMPRINT",EDGE,{"derivedFrom":makeQuery(id+"F10.opExtrude","CAP_EDGE",EDGE,{"disambiguationData":[OSD([subQ0]),TDD([makeQuery(id+"F9.imprint","IMPRINT",EDGE,{"disambiguationData":[TD([[makeQuery(id+"F9.imprint","INTERSECT",VERTEX,{"derivedFrom":[subQ0,sQuery(id+"F9.wireOp",EDGE,"E26.right")]}),-1.0]])],"derivedFrom":subQ0})])],"isStart":true})})])],"isStart":false});}
            var Q3;
            {var subQ0=sQuery(id+"F9.wireOp",EDGE,"E20");var subQ1=makeQuery(id+"F10.opExtrude","CAP_EDGE",EDGE,{"disambiguationData":[OSD([subQ0])],"isStart":true});Q3=makeQuery(id+"F14.opExtrude","CAP_EDGE",EDGE,{"disambiguationData":[OSD([subQ0]),TDD([makeQuery(id+"F13.imprint","IMPRINT",EDGE,{"disambiguationData":[TD([[makeQuery(id+"F13.imprint","INTERSECT",VERTEX,{"derivedFrom":[subQ1,sQuery(id+"F13.wireOp",EDGE,"E30")]}),1.0]])],"derivedFrom":subQ1})])],"isStart":false});}
            var Q4;
            {var subQ0=sQuery(id+"F9.wireOp",EDGE,"E24");Q4=makeQuery(id+"F14.opExtrude","CAP_EDGE",EDGE,{"disambiguationData":[OSD([subQ0]),TDD([makeQuery(id+"F13.imprint","IMPRINT",EDGE,{"derivedFrom":makeQuery(id+"F10.opExtrude","CAP_EDGE",EDGE,{"disambiguationData":[OSD([subQ0]),TDD([makeQuery(id+"F9.imprint","IMPRINT",EDGE,{"disambiguationData":[TD([[makeQuery(id+"F9.imprint","INTERSECT",VERTEX,{"disambiguationData":[OD(1.0)],"derivedFrom":[sQuery(id+"F9.wireOp",EDGE,"E22"),subQ0]}),1.0]])],"derivedFrom":subQ0})])],"isStart":true})})])],"isStart":false});}
            var Q5;
            {var subQ0=sQuery(id+"F9.wireOp",EDGE,"E21");var subQ1=makeQuery(id+"F10.opExtrude","CAP_EDGE",EDGE,{"disambiguationData":[OSD([subQ0])],"isStart":false});Q5=makeQuery(id+"F12.opExtrude","CAP_EDGE",EDGE,{"disambiguationData":[OSD([subQ0]),TDD([makeQuery(id+"F11.imprint","IMPRINT",EDGE,{"disambiguationData":[TD([[makeQuery(id+"F11.imprint","INTERSECT",VERTEX,{"derivedFrom":[subQ1,sQuery(id+"F11.wireOp",EDGE,"E28")]}),1.0]])],"derivedFrom":subQ1})])],"isStart":false});}
            var Q6;
            {var subQ0=sQuery(id+"F9.wireOp",EDGE,"E24");Q6=makeQuery(id+"F12.opExtrude","CAP_EDGE",EDGE,{"disambiguationData":[OSD([subQ0]),TDD([makeQuery(id+"F11.imprint","IMPRINT",EDGE,{"derivedFrom":makeQuery(id+"F10.opExtrude","CAP_EDGE",EDGE,{"disambiguationData":[OSD([subQ0]),TDD([makeQuery(id+"F9.imprint","IMPRINT",EDGE,{"disambiguationData":[TD([[makeQuery(id+"F9.imprint","INTERSECT",VERTEX,{"disambiguationData":[OD(1.0)],"derivedFrom":[sQuery(id+"F9.wireOp",EDGE,"E22"),subQ0]}),1.0]])],"derivedFrom":subQ0})])],"isStart":false})})])],"isStart":false});}
            var Q7;
            {var subQ0=sQuery(id+"F9.wireOp",EDGE,"E22");var subQ1=makeQuery(id+"F9.imprint","INTERSECT",VERTEX,{"derivedFrom":[sQuery(id+"F9.wireOp",EDGE,"E19"),subQ0]});Q7=makeQuery(id+"F14.opExtrude","CAP_EDGE",EDGE,{"disambiguationData":[OSD([subQ0]),TDD([makeQuery(id+"F13.imprint","IMPRINT",EDGE,{"derivedFrom":makeQuery(id+"F10.opExtrude","CAP_EDGE",EDGE,{"disambiguationData":[OSD([subQ0]),TDD([makeQuery(id+"F9.imprint","IMPRINT",EDGE,{"disambiguationData":[TD([[subQ1,1.0]])],"derivedFrom":subQ0}),makeQuery(id+"F9.imprint","IMPRINT",EDGE,{"disambiguationData":[TD([[subQ1,-1.0]])],"derivedFrom":subQ0})])],"isStart":true})})])],"isStart":false});}
            var Q8;
            {var subQ0=sQuery(id+"F9.wireOp",EDGE,"E17");var subQ1=makeQuery(id+"F9.imprint","INTERSECT",VERTEX,{"disambiguationData":[OD(0.0)],"derivedFrom":[subQ0,sQuery(id+"F9.wireOp",EDGE,"E23")]});var subQ3=makeQuery(id+"F9.imprint","INTERSECT",VERTEX,{"disambiguationData":[OD(0.0)],"derivedFrom":[subQ0,sQuery(id+"F9.wireOp",EDGE,"E24")]});Q8=makeQuery(id+"F14.opExtrude","CAP_EDGE",EDGE,{"disambiguationData":[OSD([subQ0]),TDD([makeQuery(id+"F13.imprint","IMPRINT",EDGE,{"derivedFrom":makeQuery(id+"F10.opExtrude","CAP_EDGE",EDGE,{"disambiguationData":[OSD([subQ0]),TDD([makeQuery(id+"F9.imprint","IMPRINT",EDGE,{"disambiguationData":[TD([[subQ3,1.0]])],"derivedFrom":subQ0}),makeQuery(id+"F9.imprint","IMPRINT",EDGE,{"disambiguationData":[TD([[subQ3,-1.0]])],"derivedFrom":subQ0}),makeQuery(id+"F9.imprint","IMPRINT",EDGE,{"disambiguationData":[TD([[subQ1,1.0]])],"derivedFrom":subQ0}),makeQuery(id+"F9.imprint","IMPRINT",EDGE,{"disambiguationData":[TD([[subQ1,-1.0]])],"derivedFrom":subQ0})])],"isStart":true})})])],"isStart":false});}
            var Q9;
            Q9=makeQuery(id+"F12.opExtrude","CAP_FACE",FACE,{"disambiguationData":[OSD([sQuery(id+"F9.wireOp",EDGE,"E17"),sQuery(id+"F9.wireOp",EDGE,"E20"),sQuery(id+"F9.wireOp",EDGE,"E21"),sQuery(id+"F9.wireOp",EDGE,"E22"),sQuery(id+"F9.wireOp",EDGE,"E23"),sQuery(id+"F9.wireOp",EDGE,"E24"),sQuery(id+"F11.wireOp",EDGE,"E28")])],"isStart":false});
            var Q10;
            {var subQ0=sQuery(id+"F9.wireOp",EDGE,"E17");var subQ1=makeQuery(id+"F9.imprint","INTERSECT",VERTEX,{"disambiguationData":[OD(0.0)],"derivedFrom":[subQ0,sQuery(id+"F9.wireOp",EDGE,"E23")]});var subQ3=makeQuery(id+"F9.imprint","INTERSECT",VERTEX,{"disambiguationData":[OD(0.0)],"derivedFrom":[subQ0,sQuery(id+"F9.wireOp",EDGE,"E24")]});Q10=makeQuery(id+"F12.opExtrude","CAP_EDGE",EDGE,{"disambiguationData":[OSD([subQ0]),TDD([makeQuery(id+"F11.imprint","IMPRINT",EDGE,{"derivedFrom":makeQuery(id+"F10.opExtrude","CAP_EDGE",EDGE,{"disambiguationData":[OSD([subQ0]),TDD([makeQuery(id+"F9.imprint","IMPRINT",EDGE,{"disambiguationData":[TD([[subQ3,1.0]])],"derivedFrom":subQ0}),makeQuery(id+"F9.imprint","IMPRINT",EDGE,{"disambiguationData":[TD([[subQ3,-1.0]])],"derivedFrom":subQ0}),makeQuery(id+"F9.imprint","IMPRINT",EDGE,{"disambiguationData":[TD([[subQ1,1.0]])],"derivedFrom":subQ0}),makeQuery(id+"F9.imprint","IMPRINT",EDGE,{"disambiguationData":[TD([[subQ1,-1.0]])],"derivedFrom":subQ0})])],"isStart":false})})])],"isStart":false});}
            fillet(context, id + "F16", {"entities" : qUnion([Q0, Q1, Q2, Q3, Q4, Q5, Q6, Q7, Q8, Q9, Q10]), "radius" : 0.75 * mm, "tangentPropagation" : true, "allowEdgeOverflow" : false});
        }
    });
